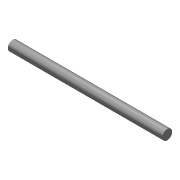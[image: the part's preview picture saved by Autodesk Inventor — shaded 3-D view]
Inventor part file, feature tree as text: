
AUTODESK INVENTOR PART (.ipt)
format: ipt  version: 2016 (Build 200138000, 138)  size: 69,120 bytes
history: native  units: in
note: dims shown in document units (in); Inventor stores cm internally (conversion verified against a paired STEP export)
features: extrude x1, sketch x1
ambient origin geometry x8: Origin, YZ Plane, XZ Plane, XY Plane, X Axis, Y Axis, Z Axis, Center Point
bodies: Solid1 (feature_tree)
feature tree (2):
  extrude  "Extrusion1"  Depth=6.875in TaperAngle=0.0deg
  sketch  "Sketch1"  dims[d0=0.4375in d1=6.875in d2=0.0in]
